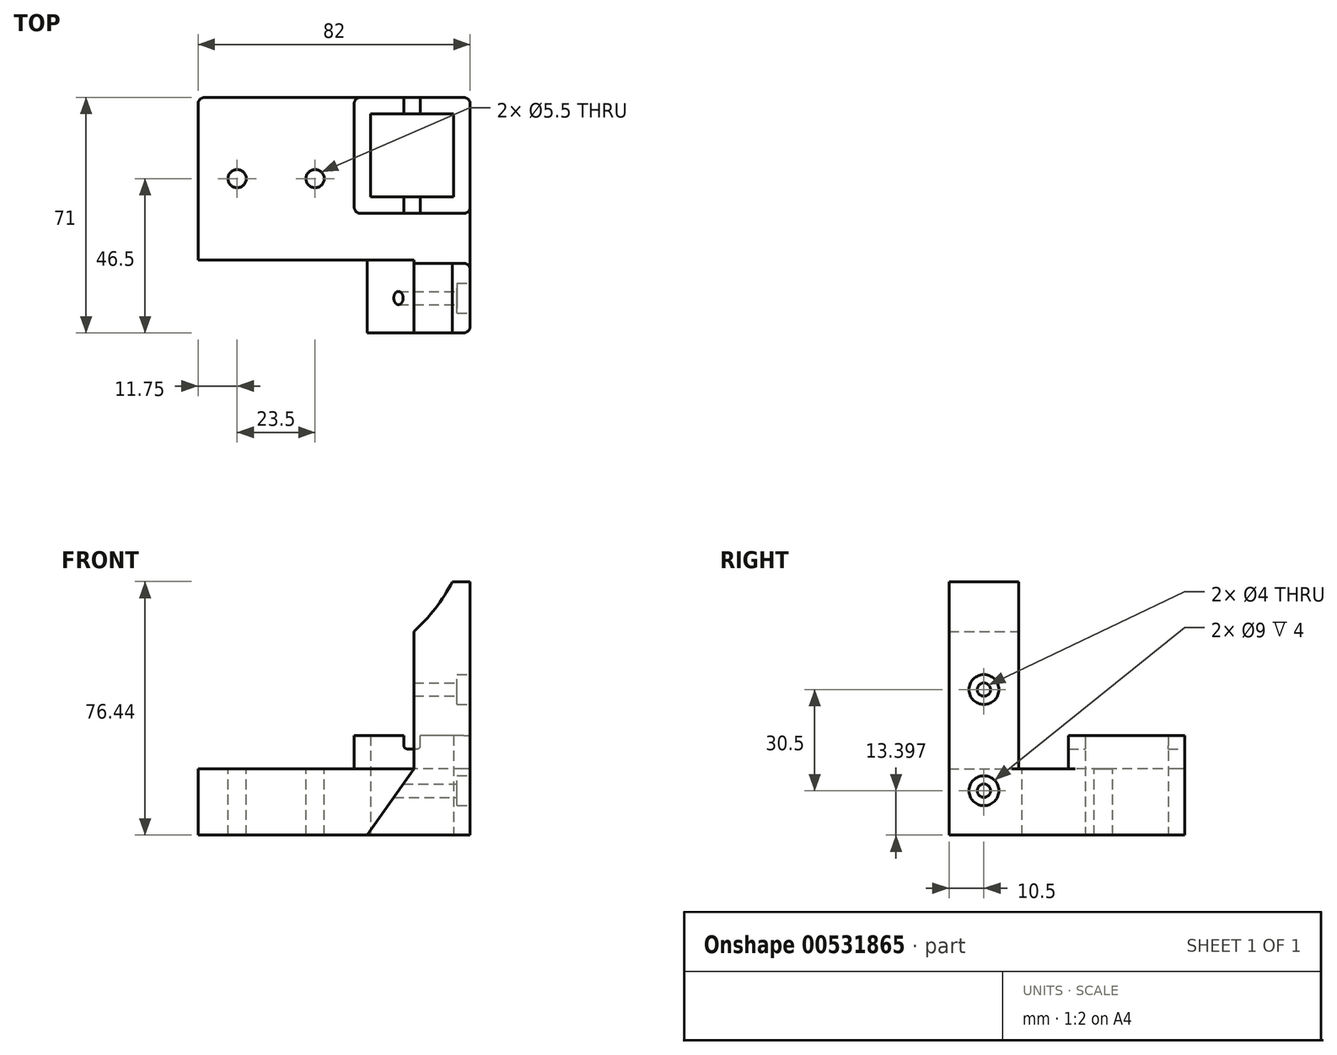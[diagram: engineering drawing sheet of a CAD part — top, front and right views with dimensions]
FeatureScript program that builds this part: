
annotation { "Feature Type Name" : "Feature", "Feature Type Description" : "" }
export const myFeature = defineFeature(function(context is Context, id is Id, definition is map)
    precondition{}
    {
        {
            var Q0;
            Q0=qCreatedBy(makeId("Front.planeOp"),FACE);
            var sketch = newSketch(context, id + "F0", { "sketchPlane" : qUnion([Q0])});
            skArc(sketch, "E0", {"start": v(33, -37.56) * mm, "mid": v(39.53, -30.62) * mm, "end": v(44.62, -22.56) * mm});
            skLineSegment(sketch, "E1.left", {"start": v(-50, -22.56) * mm, "end": v(-50, -133) * mm});
            skLineSegment(sketch, "E1.right", {"start": v(50, -22.56) * mm, "end": v(50, -133) * mm});
            skLineSegment(sketch, "E2", {"start": v(0, -99) * mm, "end": v(-33, -99) * mm});
            skLineSegment(sketch, "E3", {"start": v(33, -79) * mm, "end": v(19, -99) * mm});
            skLineSegment(sketch, "E4", {"start": v(0, -99) * mm, "end": v(19, -99) * mm});
            skLineSegment(sketch, "E5", {"start": v(-44.62, -22.56) * mm, "end": v(-50, -22.56) * mm});
            skArc(sketch, "E6.trimOffspring", {"start": v(-44.62, -22.56) * mm, "mid": v(-39.53, -30.62) * mm, "end": v(-33, -37.56) * mm});
            skLineSegment(sketch, "E7.trimOffspring", {"start": v(44.62, -22.56) * mm, "end": v(50, -22.56) * mm});
            skLineSegment(sketch, "E8.trimOffspring", {"start": v(33, -37.56) * mm, "end": v(33, -79) * mm});
            skLineSegment(sketch, "E9.trimOffspring", {"start": v(-33, -37.56) * mm, "end": v(-33, -99) * mm});
            skLineSegment(sketch, "E10.right", {"start": v(33, -150) * mm, "end": v(33, -180) * mm});
            skLineSegment(sketch, "E11.MirrorCS", {"start": v(-33, -150) * mm, "end": v(-33, -180) * mm});
            skLineSegment(sketch, "E12.MirrorCS", {"start": v(0, -197) * mm, "end": v(-33, -197) * mm});
            skLineSegment(sketch, "E13", {"start": v(33, -150) * mm, "end": v(50, -133) * mm});
            skLineSegment(sketch, "E14.MirrorCS", {"start": v(-33, -150) * mm, "end": v(-50, -133) * mm});
            skLineSegment(sketch, "E15", {"start": v(-33, -180) * mm, "end": v(-33, -197) * mm});
            skLineSegment(sketch, "E16", {"start": v(0, -197) * mm, "end": v(33, -197) * mm});
            skLineSegment(sketch, "E17", {"start": v(33, -197) * mm, "end": v(33, -180) * mm});
            skSolve(sketch);
        }
        {
            var Q0;
            Q0=qSketchRegion(id+"F0",true);
            extrude(context, id + "F1", {"entities" : qUnion([Q0]), "depth" : 21 * mm});
        }
        {
            var Q0;
            Q0=qCreatedBy(makeId("Right.planeOp"),FACE);
            var sketch = newSketch(context, id + "F2", { "sketchPlane" : qUnion([Q0])});
            skLineSegment(sketch, "E18", {"start": v(0, 0) * mm, "end": v(0, -42.6) * mm});
            skLineSegment(sketch, "E19", {"start": v(0, -42.6) * mm, "end": v(0, -67.6) * mm});
            skPoint(sketch, "E20.endSnap0", {"position": v(0, -55.1) * mm});
            skCircle(sketch, "E21", {"center": v(-10.5, -55.1) * mm, "radius": 2 * mm});
            skLineSegment(sketch, "E22", {"start": v(0, -67.6) * mm, "end": v(0, -85.6) * mm});
            skCircle(sketch, "E23", {"center": v(-10.5, -85.6) * mm, "radius": 2 * mm});
            skSolve(sketch);
        }
        {
            var Q0;
            Q0=qSketchRegion(id+"F2",true);
            extrude(context, id + "F3", {"entities" : qUnion([Q0]), "operationType" : NewBodyOperationType.REMOVE, "endBound" : BoundingType.SYMMETRIC, "oppositeDirection" : true, "depth" : 100 * mm});
        }
        {
            var Q0;
            Q0=makeQuery(id+"F1.opExtrude","SWEPT_FACE",FACE,{"disambiguationData":[OSD([sQuery(id+"F0.wireOp",EDGE,"E1.left")])]});
            var sketch = newSketch(context, id + "F4", { "sketchPlane" : qUnion([Q0])});
            skCircle(sketch, "E24", {"center": v(10.5, -55.1) * mm, "radius": 4.5 * mm});
            skCircle(sketch, "E25", {"center": v(10.5, -85.6) * mm, "radius": 4.5 * mm});
            skSolve(sketch);
        }
        {
            var Q0;
            Q0=qSketchRegion(id+"F4",true);
            extrude(context, id + "F5", {"entities" : qUnion([Q0]), "operationType" : NewBodyOperationType.REMOVE, "oppositeDirection" : true, "depth" : 4 * mm});
        }
        {
            var Q0;
            Q0=makeQuery(id+"F1.opExtrude","SWEPT_FACE",FACE,{"disambiguationData":[OSD([sQuery(id+"F0.wireOp",EDGE,"E1.right")])]});
            var sketch = newSketch(context, id + "F6", { "sketchPlane" : qUnion([Q0])});
            skCircle(sketch, "E26", {"center": v(-10.5, -55.1) * mm, "radius": 4.5 * mm});
            skCircle(sketch, "E27", {"center": v(-10.5, -85.6) * mm, "radius": 4.5 * mm});
            skSolve(sketch);
        }
        {
            var Q0;
            Q0=qSketchRegion(id+"F6",true);
            extrude(context, id + "F7", {"entities" : qUnion([Q0]), "operationType" : NewBodyOperationType.REMOVE, "oppositeDirection" : true, "depth" : 4 * mm});
        }
        {
            var Q0;
            Q0=makeQuery(id+"F1.opExtrude","SWEPT_FACE",FACE,{"disambiguationData":[OSD([sQuery(id+"F0.wireOp",EDGE,"E12.MirrorCS"),sQuery(id+"F0.wireOp",EDGE,"E16")])]});
            var sketch = newSketch(context, id + "F8", { "sketchPlane" : qUnion([Q0])});
            skLineSegment(sketch, "E28", {"start": v(-33, 10.5) * mm, "end": v(-21, 10.5) * mm});
            skLineSegment(sketch, "E29", {"start": v(33, 10.5) * mm, "end": v(21, 10.5) * mm});
            skCircle(sketch, "E30", {"center": v(-21, 10.5) * mm, "radius": 2 * mm});
            skCircle(sketch, "E31", {"center": v(21, 10.5) * mm, "radius": 2 * mm});
            skSolve(sketch);
        }
        {
            var Q0;
            Q0=qSketchRegion(id+"F8",true);
            extrude(context, id + "F9", {"entities" : qUnion([Q0]), "operationType" : NewBodyOperationType.REMOVE, "oppositeDirection" : true, "depth" : 15 * mm});
        }
        {
            var Q0;
            Q0=makeQuery(id+"F1.opExtrude","CAP_FACE",FACE,{"disambiguationData":[OSD([sQuery(id+"F0.wireOp",EDGE,"E0"),sQuery(id+"F0.wireOp",EDGE,"E1.left"),sQuery(id+"F0.wireOp",EDGE,"E1.right"),sQuery(id+"F0.wireOp",EDGE,"E2"),sQuery(id+"F0.wireOp",EDGE,"E3"),sQuery(id+"F0.wireOp",EDGE,"E4"),sQuery(id+"F0.wireOp",EDGE,"E5"),sQuery(id+"F0.wireOp",EDGE,"E6.trimOffspring"),sQuery(id+"F0.wireOp",EDGE,"E7.trimOffspring"),sQuery(id+"F0.wireOp",EDGE,"E8.trimOffspring"),sQuery(id+"F0.wireOp",EDGE,"E9.trimOffspring"),sQuery(id+"F0.wireOp",EDGE,"E10.right"),sQuery(id+"F0.wireOp",EDGE,"E11.MirrorCS"),sQuery(id+"F0.wireOp",EDGE,"E12.MirrorCS"),sQuery(id+"F0.wireOp",EDGE,"E13"),sQuery(id+"F0.wireOp",EDGE,"E14.MirrorCS"),sQuery(id+"F0.wireOp",EDGE,"E15"),sQuery(id+"F0.wireOp",EDGE,"E16"),sQuery(id+"F0.wireOp",EDGE,"E17")])],"isStart":false});
            var sketch = newSketch(context, id + "F10", { "sketchPlane" : qUnion([Q0])});
            skLineSegment(sketch, "E32", {"start": v(0, -197) * mm, "end": v(0, -140) * mm});
            skPoint(sketch, "E32.endSnap0", {"position": v(0, -197) * mm});
            skLineSegment(sketch, "E33", {"start": v(0, -140) * mm, "end": v(0, -126) * mm});
            skCircle(sketch, "E34", {"center": v(0, -168.5) * mm, "radius": 2 * mm});
            skCircle(sketch, "E35", {"center": v(0, -133) * mm, "radius": 2 * mm});
            skSolve(sketch);
        }
        {
            var Q0;
            Q0=qSketchRegion(id+"F10",true);
            extrude(context, id + "F11", {"entities" : qUnion([Q0]), "operationType" : NewBodyOperationType.REMOVE, "oppositeDirection" : true, "depth" : 12 * mm});
        }
        {
            var Q0;
            Q0=makeQuery(id+"F1.opExtrude","CAP_FACE",FACE,{"disambiguationData":[OSD([sQuery(id+"F0.wireOp",EDGE,"E0"),sQuery(id+"F0.wireOp",EDGE,"E1.left"),sQuery(id+"F0.wireOp",EDGE,"E1.right"),sQuery(id+"F0.wireOp",EDGE,"E2"),sQuery(id+"F0.wireOp",EDGE,"E3"),sQuery(id+"F0.wireOp",EDGE,"E4"),sQuery(id+"F0.wireOp",EDGE,"E5"),sQuery(id+"F0.wireOp",EDGE,"E6.trimOffspring"),sQuery(id+"F0.wireOp",EDGE,"E7.trimOffspring"),sQuery(id+"F0.wireOp",EDGE,"E8.trimOffspring"),sQuery(id+"F0.wireOp",EDGE,"E9.trimOffspring"),sQuery(id+"F0.wireOp",EDGE,"E10.right"),sQuery(id+"F0.wireOp",EDGE,"E11.MirrorCS"),sQuery(id+"F0.wireOp",EDGE,"E12.MirrorCS"),sQuery(id+"F0.wireOp",EDGE,"E13"),sQuery(id+"F0.wireOp",EDGE,"E14.MirrorCS"),sQuery(id+"F0.wireOp",EDGE,"E15"),sQuery(id+"F0.wireOp",EDGE,"E16"),sQuery(id+"F0.wireOp",EDGE,"E17")])],"isStart":false});
            var sketch = newSketch(context, id + "F12", { "sketchPlane" : qUnion([Q0])});
            skLineSegment(sketch, "E36.bottom", {"start": v(19, -99) * mm, "end": v(101.71, -99) * mm});
            skLineSegment(sketch, "E36.top", {"start": v(19, -204.05) * mm, "end": v(101.71, -204.05) * mm});
            skLineSegment(sketch, "E36.left", {"start": v(19, -99) * mm, "end": v(19, -204.05) * mm});
            skLineSegment(sketch, "E36.right", {"start": v(101.71, -99) * mm, "end": v(101.71, -204.05) * mm});
            skLineSegment(sketch, "E37.bottom", {"start": v(19, -99) * mm, "end": v(-74.74, -99) * mm});
            skLineSegment(sketch, "E37.top", {"start": v(19, -204.05) * mm, "end": v(-74.74, -204.05) * mm});
            skLineSegment(sketch, "E37.right", {"start": v(-74.74, -99) * mm, "end": v(-74.74, -204.05) * mm});
            skLineSegment(sketch, "E38.top", {"start": v(19, -14.53) * mm, "end": v(-74.74, -14.53) * mm});
            skLineSegment(sketch, "E38.left", {"start": v(19, -99) * mm, "end": v(19, -14.53) * mm});
            skLineSegment(sketch, "E38.right", {"start": v(-74.74, -99) * mm, "end": v(-74.74, -14.53) * mm});
            skSolve(sketch);
        }
        {
            var Q0;
            Q0=qSketchRegion(id+"F12",true);
            extrude(context, id + "F13", {"entities" : qUnion([Q0]), "operationType" : NewBodyOperationType.REMOVE, "oppositeDirection" : true, "depth" : 25 * mm});
        }
        {
            var Q0;
            Q0=makeQuery(id+"F1.opExtrude","CAP_FACE",FACE,{"disambiguationData":[OSD([sQuery(id+"F0.wireOp",EDGE,"E0"),sQuery(id+"F0.wireOp",EDGE,"E1.left"),sQuery(id+"F0.wireOp",EDGE,"E1.right"),sQuery(id+"F0.wireOp",EDGE,"E2"),sQuery(id+"F0.wireOp",EDGE,"E3"),sQuery(id+"F0.wireOp",EDGE,"E4"),sQuery(id+"F0.wireOp",EDGE,"E5"),sQuery(id+"F0.wireOp",EDGE,"E6.trimOffspring"),sQuery(id+"F0.wireOp",EDGE,"E7.trimOffspring"),sQuery(id+"F0.wireOp",EDGE,"E8.trimOffspring"),sQuery(id+"F0.wireOp",EDGE,"E9.trimOffspring"),sQuery(id+"F0.wireOp",EDGE,"E10.right"),sQuery(id+"F0.wireOp",EDGE,"E11.MirrorCS"),sQuery(id+"F0.wireOp",EDGE,"E12.MirrorCS"),sQuery(id+"F0.wireOp",EDGE,"E13"),sQuery(id+"F0.wireOp",EDGE,"E14.MirrorCS"),sQuery(id+"F0.wireOp",EDGE,"E15"),sQuery(id+"F0.wireOp",EDGE,"E16"),sQuery(id+"F0.wireOp",EDGE,"E17")])],"isStart":true});
            var sketch = newSketch(context, id + "F14", { "sketchPlane" : qUnion([Q0])});
            skLineSegment(sketch, "E39.bottom", {"start": v(-50, -99) * mm, "end": v(24.02, -99) * mm});
            skLineSegment(sketch, "E39.top", {"start": v(-50, -79) * mm, "end": v(24.02, -79) * mm});
            skLineSegment(sketch, "E39.left", {"start": v(-50, -99) * mm, "end": v(-50, -79) * mm});
            skLineSegment(sketch, "E40", {"start": v(-33, -79) * mm, "end": v(32, -79) * mm});
            skLineSegment(sketch, "E41", {"start": v(32, -79) * mm, "end": v(32, -99) * mm});
            skLineSegment(sketch, "E42", {"start": v(32, -99) * mm, "end": v(24.02, -99) * mm});
            skSolve(sketch);
        }
        {
            var Q0;
            Q0=qSketchRegion(id+"F14",true);
            extrude(context, id + "F15", {"entities" : qUnion([Q0]), "operationType" : NewBodyOperationType.ADD, "depth" : 50 * mm});
        }
        {
            var Q0;
            Q0=makeQuery(id+"F15.opExtrude","SWEPT_FACE",FACE,{"disambiguationData":[OSD([sQuery(id+"F14.wireOp",EDGE,"E41")])]});
            var sketch = newSketch(context, id + "F16", { "sketchPlane" : qUnion([Q0])});
            skLineSegment(sketch, "E43.bottom", {"start": v(0, -79) * mm, "end": v(-1, -79) * mm});
            skLineSegment(sketch, "E43.top", {"start": v(0, -99) * mm, "end": v(-1, -99) * mm});
            skLineSegment(sketch, "E43.left", {"start": v(0, -79) * mm, "end": v(0, -99) * mm});
            skLineSegment(sketch, "E43.right", {"start": v(-1, -79) * mm, "end": v(-1, -99) * mm});
            skSolve(sketch);
        }
        {
            var Q0;
            Q0=qSketchRegion(id+"F16",true);
            extrude(context, id + "F17", {"entities" : qUnion([Q0]), "operationType" : NewBodyOperationType.REMOVE, "oppositeDirection" : true, "depth" : 65 * mm});
        }
        {
            var Q0;
            Q0=makeQuery(id+"F17.boolean.opBoolean","COPY",FACE,{"derivedFrom":makeQuery(id+"F17.opExtrude","SWEPT_FACE",FACE,{"disambiguationData":[OSD([sQuery(id+"F16.wireOp",EDGE,"E43.left")])]})});
            extrude(context, id + "F18", {"entities" : qUnion([Q0]), "operationType" : NewBodyOperationType.ADD, "depth" : 25 * mm});
        }
        {
            var Q0;
            Q0=makeQuery(id+"F15.opExtrude","SWEPT_FACE",FACE,{"disambiguationData":[OSD([sQuery(id+"F14.wireOp",EDGE,"E39.top"),sQuery(id+"F14.wireOp",EDGE,"E40")])]});
            var sketch = newSketch(context, id + "F19", { "sketchPlane" : qUnion([Q0])});
            skLineSegment(sketch, "E44.bottom", {"start": v(50, 50) * mm, "end": v(15, 50) * mm});
            skLineSegment(sketch, "E44.top", {"start": v(50, 15) * mm, "end": v(15, 15) * mm});
            skLineSegment(sketch, "E44.left", {"start": v(50, 50) * mm, "end": v(50, 15) * mm});
            skLineSegment(sketch, "E44.right", {"start": v(15, 50) * mm, "end": v(15, 15) * mm});
            skLineSegment(sketch, "E45.bottom", {"start": v(45, 45) * mm, "end": v(20, 45) * mm});
            skLineSegment(sketch, "E45.top", {"start": v(45, 20) * mm, "end": v(20, 20) * mm});
            skLineSegment(sketch, "E45.left", {"start": v(45, 45) * mm, "end": v(45, 20) * mm});
            skLineSegment(sketch, "E45.right", {"start": v(20, 45) * mm, "end": v(20, 20) * mm});
            skPoint(sketch, "E45.middle", {"position": v(32.5, 32.5) * mm});
            skPoint(sketch, "E45.middle.positionSnap0", {"position": v(15, 32.5) * mm});
            skPoint(sketch, "E45.middle.positionSnap1", {"position": v(32.5, 50) * mm});
            skPoint(sketch, "E45.centerSnap0", {"position": v(15, 32.5) * mm});
            skPoint(sketch, "E45.centerSnap1", {"position": v(32.5, 50) * mm});
            skSolve(sketch);
        }
        {
            var Q0;
            Q0=qSketchRegion(id+"F19",true);
            extrude(context, id + "F20", {"entities" : qUnion([Q0]), "operationType" : NewBodyOperationType.ADD, "depth" : 10 * mm});
        }
        {
            var Q0;
            Q0=makeQuery(id+"F20.boolean.opBoolean","SPLIT",FACE,{"disambiguationData":[TD([makeQuery(id+"F20.opExtrude","SWEPT_FACE",FACE,{"disambiguationData":[OSD([sQuery(id+"F19.wireOp",EDGE,"E45.bottom")])]})])],"derivedFrom":makeQuery(id+"F15.opExtrude","SWEPT_FACE",FACE,{"disambiguationData":[OSD([sQuery(id+"F14.wireOp",EDGE,"E39.top"),sQuery(id+"F14.wireOp",EDGE,"E40")])]})});
            extrude(context, id + "F21", {"entities" : qUnion([Q0]), "operationType" : NewBodyOperationType.REMOVE, "oppositeDirection" : true, "depth" : 25 * mm});
        }
        {
            var Q0;
            Q0=makeQuery(id+"F20.boolean.opBoolean","MERGE",FACE,{"derivedFrom":[makeQuery(id+"F15.opExtrude","CAP_FACE",FACE,{"disambiguationData":[OSD([sQuery(id+"F14.wireOp",EDGE,"E39.bottom"),sQuery(id+"F14.wireOp",EDGE,"E39.top"),sQuery(id+"F14.wireOp",EDGE,"E39.left"),sQuery(id+"F14.wireOp",EDGE,"E40"),sQuery(id+"F14.wireOp",EDGE,"E41"),sQuery(id+"F14.wireOp",EDGE,"E42")])],"isStart":false}),makeQuery(id+"F20.opExtrude","SWEPT_FACE",FACE,{"disambiguationData":[OSD([sQuery(id+"F19.wireOp",EDGE,"E44.bottom")])]})]});
            var sketch = newSketch(context, id + "F22", { "sketchPlane" : qUnion([Q0])});
            skLineSegment(sketch, "E46.bottom", {"start": v(-30, -73) * mm, "end": v(-35, -73) * mm});
            skLineSegment(sketch, "E46.top", {"start": v(-30, -65) * mm, "end": v(-35, -65) * mm});
            skLineSegment(sketch, "E46.left", {"start": v(-30, -73) * mm, "end": v(-30, -65) * mm});
            skLineSegment(sketch, "E46.right", {"start": v(-35, -73) * mm, "end": v(-35, -65) * mm});
            skPoint(sketch, "E46.middle", {"position": v(-32.5, -69) * mm});
            skSolve(sketch);
        }
        {
            var Q0;
            Q0=qSketchRegion(id+"F22",true);
            extrude(context, id + "F23", {"entities" : qUnion([Q0]), "operationType" : NewBodyOperationType.REMOVE, "oppositeDirection" : true, "depth" : 41 * mm});
        }
        {
            var Q0;
            {var subQ0=sQuery(id+"F22.wireOp",EDGE,"E46.bottom");var subQ2=sQuery(id+"F22.wireOp",EDGE,"E46.right");Q0=makeQuery(id+"F23.boolean.opBoolean","COPY",EDGE,{"disambiguationData":[TD([makeQuery(id+"F20.opExtrude","SWEPT_FACE",FACE,{"disambiguationData":[OSD([sQuery(id+"F19.wireOp",EDGE,"E44.top")])]})])],"derivedFrom":makeQuery(id+"F23.opExtrude","SWEPT_EDGE",EDGE,{"disambiguationData":[OSD([subQ0,subQ2])]})});}
            var Q1;
            {var subQ0=sQuery(id+"F22.wireOp",EDGE,"E46.bottom");var subQ2=sQuery(id+"F22.wireOp",EDGE,"E46.left");Q1=makeQuery(id+"F23.boolean.opBoolean","COPY",EDGE,{"disambiguationData":[TD([makeQuery(id+"F20.opExtrude","SWEPT_FACE",FACE,{"disambiguationData":[OSD([sQuery(id+"F19.wireOp",EDGE,"E44.top")])]})])],"derivedFrom":makeQuery(id+"F23.opExtrude","SWEPT_EDGE",EDGE,{"disambiguationData":[OSD([subQ0,subQ2])]})});}
            var Q2;
            {var subQ1=sQuery(id+"F22.wireOp",EDGE,"E46.bottom");var subQ2=sQuery(id+"F22.wireOp",EDGE,"E46.right");Q2=makeQuery(id+"F23.boolean.opBoolean","COPY",EDGE,{"disambiguationData":[TD([makeQuery(id+"F20.opExtrude","SWEPT_FACE",FACE,{"disambiguationData":[OSD([sQuery(id+"F19.wireOp",EDGE,"E44.bottom")])]})])],"derivedFrom":makeQuery(id+"F23.opExtrude","SWEPT_EDGE",EDGE,{"disambiguationData":[OSD([subQ1,subQ2])]})});}
            var Q3;
            {var subQ1=sQuery(id+"F22.wireOp",EDGE,"E46.left");var subQ2=sQuery(id+"F22.wireOp",EDGE,"E46.bottom");Q3=makeQuery(id+"F23.boolean.opBoolean","COPY",EDGE,{"disambiguationData":[TD([makeQuery(id+"F20.opExtrude","SWEPT_FACE",FACE,{"disambiguationData":[OSD([sQuery(id+"F19.wireOp",EDGE,"E44.bottom")])]})])],"derivedFrom":makeQuery(id+"F23.opExtrude","SWEPT_EDGE",EDGE,{"disambiguationData":[OSD([subQ2,subQ1])]})});}
            fillet(context, id + "F24", {"entities" : qUnion([Q0, Q1, Q2, Q3]), "radius" : 1 * mm, "tangentPropagation" : true, "allowEdgeOverflow" : false});
        }
        {
            var Q0;
            {var subQ2=sQuery(id+"F14.wireOp",EDGE,"E40");var subQ4=sQuery(id+"F14.wireOp",EDGE,"E39.top");var subQ6=sQuery(id+"F0.wireOp",EDGE,"E1.right");Q0=makeQuery(id+"F20.boolean.opBoolean","SPLIT",FACE,{"disambiguationData":[TD([makeQuery(id+"F1.opExtrude","SWEPT_FACE",FACE,{"disambiguationData":[OSD([subQ6])]})])],"derivedFrom":makeQuery(id+"F15.opExtrude","SWEPT_FACE",FACE,{"disambiguationData":[OSD([subQ4,subQ2])]})});}
            var sketch = newSketch(context, id + "F25", { "sketchPlane" : qUnion([Q0])});
            skLineSegment(sketch, "E47", {"start": v(-32, 25.5) * mm, "end": v(-8.5, 25.5) * mm});
            skLineSegment(sketch, "E48", {"start": v(-8.5, 25.5) * mm, "end": v(-8.5, 42.4) * mm});
            skPoint(sketch, "E49.orphan", {"position": v(15, 25.5) * mm});
            skCircle(sketch, "E50", {"center": v(-20.25, 25.5) * mm, "radius": 2.75 * mm});
            skCircle(sketch, "E51.MirrorC", {"center": v(3.25, 25.5) * mm, "radius": 2.75 * mm});
            skSolve(sketch);
        }
        {
            var Q0;
            Q0=qSketchRegion(id+"F25",true);
            extrude(context, id + "F26", {"entities" : qUnion([Q0]), "operationType" : NewBodyOperationType.REMOVE, "oppositeDirection" : true, "depth" : 25 * mm});
        }
        {
            var Q0;
            Q0=makeQuery(id+"F1.opExtrude","CAP_EDGE",EDGE,{"disambiguationData":[OSD([sQuery(id+"F0.wireOp",EDGE,"E1.right")])],"isStart":false});
            var Q1;
            Q1=makeQuery(id+"F1.opExtrude","CAP_EDGE",EDGE,{"disambiguationData":[OSD([sQuery(id+"F0.wireOp",EDGE,"E1.right")])],"isStart":true});
            var Q2;
            Q2=makeQuery(id+"F20.boolean.opBoolean","MERGE",EDGE,{"derivedFrom":[makeQuery(id+"F15.opExtrude","CAP_EDGE",EDGE,{"disambiguationData":[OSD([sQuery(id+"F14.wireOp",EDGE,"E39.left")])],"isStart":false}),makeQuery(id+"F20.opExtrude","SWEPT_EDGE",EDGE,{"disambiguationData":[OSD([sQuery(id+"F19.wireOp",EDGE,"E44.bottom"),sQuery(id+"F19.wireOp",EDGE,"E44.left")])]})]});
            var Q3;
            Q3=makeQuery(id+"F20.opExtrude","SWEPT_EDGE",EDGE,{"disambiguationData":[OSD([sQuery(id+"F0.wireOp",EDGE,"E1.right"),sQuery(id+"F14.wireOp",EDGE,"E39.top"),sQuery(id+"F14.wireOp",EDGE,"E39.left"),sQuery(id+"F19.wireOp",EDGE,"E44.top"),sQuery(id+"F19.wireOp",EDGE,"E44.left")])]});
            var Q4;
            Q4=makeQuery(id+"F20.opExtrude","SWEPT_EDGE",EDGE,{"disambiguationData":[OSD([sQuery(id+"F14.wireOp",EDGE,"E39.top"),sQuery(id+"F14.wireOp",EDGE,"E40"),sQuery(id+"F19.wireOp",EDGE,"E44.bottom"),sQuery(id+"F19.wireOp",EDGE,"E44.right")])]});
            var Q5;
            Q5=makeQuery(id+"F20.opExtrude","SWEPT_EDGE",EDGE,{"disambiguationData":[OSD([sQuery(id+"F19.wireOp",EDGE,"E44.top"),sQuery(id+"F19.wireOp",EDGE,"E44.right")])]});
            var Q6;
            Q6=makeQuery(id+"F15.opExtrude","CAP_EDGE",EDGE,{"disambiguationData":[OSD([sQuery(id+"F14.wireOp",EDGE,"E41")])],"isStart":false});
            var Q7;
            Q7=makeQuery(id+"F17.boolean.opBoolean","COPY",EDGE,{"derivedFrom":makeQuery(id+"F17.opExtrude","CAP_EDGE",EDGE,{"disambiguationData":[OSD([sQuery(id+"F16.wireOp",EDGE,"E43.right")])],"isStart":true})});
            fillet(context, id + "F27", {"entities" : qUnion([Q0, Q1, Q2, Q3, Q4, Q5, Q6, Q7]), "radius" : 2 * mm, "tangentPropagation" : true, "allowEdgeOverflow" : false});
        }
    });
